FCSTD DOCUMENT  (FreeCAD 0.20R29177 +426 (Git))
Label: X2SON-5_0.8x0.8mm_P0.48mm
License: All rights reserved
LicenseURL: http://en.wikipedia.org/wiki/All_rights_reserved
objects: Sketcher::SketchObject×14, App::Annotation×2, Part::Offset2D×2, App::DocumentObjectGroup×1
note: 16 computed .brp shape members not serialized (recipe doc carries the construction recipe); baked Part::Feature solids carry a one-line shape summary decoded from their .brp

FEATURE [Sketcher::SketchObject] Sketch  label="Pads_Poly_Mask1"
  FullyConstrained = true
  sketch-geometry (12):
    g0: LineSegment StartX=-0.55 StartY=0.13 StartZ=0 EndX=-0.34 EndY=0.13 EndZ=0
    g1: LineSegment StartX=-0.34 StartY=0.13 StartZ=0 EndX=-0.18 EndY=0.29 EndZ=0
    g2: LineSegment StartX=-0.18 StartY=0.29 StartZ=0 EndX=-0.18 EndY=0.35 EndZ=0
    g3: LineSegment StartX=-0.18 StartY=0.35 StartZ=0 EndX=-0.55 EndY=0.35 EndZ=0
    g4: LineSegment StartX=-0.6 StartY=0.3 StartZ=0 EndX=-0.6 EndY=0.18 EndZ=0
    g5: LineSegment StartX=-0.39 StartY=0.35 StartZ=0 EndX=-0.39 EndY=0.13 EndZ=0
    g6: LineSegment StartX=-0.6 StartY=0.24 StartZ=0 EndX=-0.23 EndY=0.24 EndZ=0
    g7: Circle CenterX=-0.39 CenterY=0.24 CenterZ=0 NormalX=0 NormalY=0 NormalZ=1 AngleXU=0 Radius=0.025
    g8: ArcOfCircle CenterX=-0.55 CenterY=0.3 CenterZ=0 NormalX=0 NormalY=0 NormalZ=1 AngleXU=0 Radius=0.05 StartAngle=1.5708 EndAngle=3.14159
    g9: GeomPoint X=-0.6 Y=0.35 Z=0
    g10: ArcOfCircle CenterX=-0.55 CenterY=0.18 CenterZ=0 NormalX=0 NormalY=0 NormalZ=1 AngleXU=0 Radius=0.05 StartAngle=3.14159 EndAngle=4.71239
    g11: GeomPoint X=-0.6 Y=0.13 Z=0
  constraints (32):
    c: Horizontal(g0)
    c: Coincident(g0,g1)
    c: Coincident(g1,g2)
    c: Vertical(g2)
    c: Coincident(g2,g3)
    c: Horizontal(g3)
    c: Vertical(g4)
    c: Distance(g3,g9) = 0.42
    c: Distance(g0,g11) = 0.26
    c: Distance(g11,g9) = 0.22
    c: Distance(g2) = 0.06
    c: PointOnObject(g5,g0)
    c: Vertical(g5)
    c: Symmetric(g3,g9,g5)
    c: PointOnObject(g6,g1)
    c: Horizontal(g6)
    c: Symmetric(g9,g11,g6)
    c: Distance(g6,g-1) = 0.24
    c: PointOnObject(g7,g6)
    c: PointOnObject(g7,g5)
    c: Diameter(g7) = 0.05
    c: PointOnObject(g9,g3)
    c: PointOnObject(g9,g4)
    c: Tangent(g3,g8) = -1.5708
    c: Tangent(g4,g8) = -1.5708
    c: PointOnObject(g11,g4)
    c: PointOnObject(g11,g0)
    c: Tangent(g4,g10) = -1.5708
    c: Tangent(g0,g10) = -1.5708
    c: Radius(g10) = 0.05
    c: Radius(g8) = 0.05
    c: Distance(g5,g-2) = 0.39
FEATURE [App::Annotation] Text  label="Ref#_1.0mm"
  LabelText = REF**
  Position = (0,1.5,0)
FEATURE [App::Annotation] Text001  label="Value#_0.6mm"
  LabelText = X2SON-4_0.8x0.8mm_P0.48mm
  Position = (0,-1.5,0)
FEATURE [Sketcher::SketchObject] Sketch001  label="Pads_Poly_Mask3"
  FullyConstrained = true
  sketch-geometry (13):
    g0: LineSegment StartX=-0.141421 StartY=0.0353553 StartZ=0 EndX=-0.0353553 EndY=0.141421 EndZ=0
    g1: LineSegment StartX=0.0353553 StartY=0.141421 StartZ=0 EndX=0.141421 EndY=0.0353553 EndZ=0
    g2: LineSegment StartX=0.141421 StartY=-0.0353553 StartZ=0 EndX=0.0353553 EndY=-0.141421 EndZ=0
    g3: LineSegment StartX=-0.0353553 StartY=-0.141421 StartZ=0 EndX=-0.141421 EndY=-0.0353553 EndZ=0
    g4: ArcOfCircle CenterX=0 CenterY=0.106066 CenterZ=0 NormalX=0 NormalY=0 NormalZ=1 AngleXU=0 Radius=0.05 StartAngle=0.785398 EndAngle=2.35619
    g5: GeomPoint X=0 Y=0.176777 Z=0
    g6: ArcOfCircle CenterX=-0.106066 CenterY=-1e-16 CenterZ=0 NormalX=0 NormalY=0 NormalZ=1 AngleXU=0 Radius=0.05 StartAngle=2.35619 EndAngle=3.92699
    g7: GeomPoint X=-0.176777 Y=0 Z=0
    g8: ArcOfCircle CenterX=0 CenterY=-0.106066 CenterZ=0 NormalX=0 NormalY=0 NormalZ=1 AngleXU=0 Radius=0.05 StartAngle=3.92699 EndAngle=5.49779
    g9: GeomPoint X=0 Y=-0.176777 Z=0
    g10: ArcOfCircle CenterX=0.106066 CenterY=0 CenterZ=0 NormalX=0 NormalY=0 NormalZ=1 AngleXU=0 Radius=0.05 StartAngle=5.49779 EndAngle=7.06858
    g11: GeomPoint X=0.176777 Y=0 Z=0
    g12: Circle CenterX=0 CenterY=0 CenterZ=0 NormalX=0 NormalY=0 NormalZ=1 AngleXU=0 Radius=0.025
  constraints (31):
    c: PointOnObject(g7,g-1)
    c: PointOnObject(g5,g-2)
    c: PointOnObject(g11,g-1)
    c: PointOnObject(g9,g-2)
    c: Perpendicular(g1,g0)
    c: Perpendicular(g2,g1)
    c: Perpendicular(g3,g2)
    c: Distance(g11,g5) = 0.25
    c: PointOnObject(g5,g0)
    c: PointOnObject(g5,g1)
    c: Tangent(g0,g4) = 1.5708
    c: Tangent(g1,g4) = 1.5708
    c: Radius(g4) = 0.05
    c: PointOnObject(g7,g0)
    c: PointOnObject(g7,g3)
    c: Tangent(g0,g6) = 1.5708
    c: Tangent(g3,g6) = 1.5708
    c: PointOnObject(g9,g3)
    c: PointOnObject(g9,g2)
    c: Tangent(g3,g8) = 1.5708
    c: Tangent(g2,g8) = 1.5708
    c: PointOnObject(g11,g2)
    c: PointOnObject(g11,g1)
    c: Tangent(g2,g10) = 1.5708
    c: Tangent(g1,g10) = 1.5708
    c: Equal(g4,g10)
    c: Equal(g4,g8)
    c: Equal(g4,g6)
    c: Coincident(g12,g-1)
    c: Diameter(g12) = 0.05
    c: Distance(g1,g3) = 0.25
FEATURE [Sketcher::SketchObject] MirroredSketch001  label="Pads_Poly_Mask5"
  FullyConstrained = true
  sketch-geometry (12):
    g0: LineSegment StartX=0.55 StartY=0.13 StartZ=0 EndX=0.34 EndY=0.13 EndZ=0
    g1: LineSegment StartX=0.34 StartY=0.13 StartZ=0 EndX=0.18 EndY=0.29 EndZ=0
    g2: LineSegment StartX=0.18 StartY=0.29 StartZ=0 EndX=0.18 EndY=0.35 EndZ=0
    g3: LineSegment StartX=0.18 StartY=0.35 StartZ=0 EndX=0.55 EndY=0.35 EndZ=0
    g4: LineSegment StartX=0.6 StartY=0.3 StartZ=0 EndX=0.6 EndY=0.18 EndZ=0
    g5: LineSegment StartX=0.39 StartY=0.35 StartZ=0 EndX=0.39 EndY=0.13 EndZ=0
    g6: LineSegment StartX=0.6 StartY=0.24 StartZ=0 EndX=0.23 EndY=0.24 EndZ=0
    g7: Circle CenterX=0.39 CenterY=0.24 CenterZ=0 NormalX=0 NormalY=0 NormalZ=1 AngleXU=0 Radius=0.025
    g8: ArcOfCircle CenterX=0.55 CenterY=0.3 CenterZ=0 NormalX=0 NormalY=0 NormalZ=1 AngleXU=0 Radius=0.05 StartAngle=0 EndAngle=1.5708
    g9: GeomPoint X=0.6 Y=0.35 Z=0
    g10: ArcOfCircle CenterX=0.55 CenterY=0.18 CenterZ=0 NormalX=0 NormalY=0 NormalZ=1 AngleXU=0 Radius=0.05 StartAngle=4.71239 EndAngle=6.28319
    g11: GeomPoint X=0.6 Y=0.13 Z=0
  constraints (32):
    c: Horizontal(g0)
    c: Coincident(g0,g1)
    c: Coincident(g1,g2)
    c: Vertical(g2)
    c: Coincident(g2,g3)
    c: Horizontal(g3)
    c: Vertical(g4)
    c: Distance(g3,g9) = 0.42
    c: Distance(g0,g11) = 0.26
    c: Distance(g11,g9) = 0.22
    c: Distance(g2) = 0.06
    c: PointOnObject(g5,g0)
    c: Vertical(g5)
    c: Symmetric(g3,g9,g5)
    c: PointOnObject(g6,g1)
    c: Horizontal(g6)
    c: Symmetric(g9,g11,g6)
    c: PointOnObject(g7,g6)
    c: PointOnObject(g7,g5)
    c: Diameter(g7) = 0.05
    c: PointOnObject(g9,g3)
    c: PointOnObject(g9,g4)
    c: Tangent(g3,g8) = 1.5708
    c: Tangent(g4,g8) = 1.5708
    c: PointOnObject(g11,g4)
    c: PointOnObject(g11,g0)
    c: Tangent(g4,g10) = 1.5708
    c: Tangent(g0,g10) = 1.5708
    c: Radius(g10) = 0.05
    c: Radius(g8) = 0.05
    c: Distance(g5,g-2) = 0.39
    c: Distance(g6,g-1) = 0.24
FEATURE [Sketcher::SketchObject] Sketch003  label="Pads_TH_SMD_padNum=3"
  FullyConstrained = true
  sketch-geometry (2):
    g0: Circle CenterX=0 CenterY=0 CenterZ=0 NormalX=0 NormalY=0 NormalZ=1 AngleXU=0 Radius=0.051
    g1: Circle CenterX=0 CenterY=0 CenterZ=0 NormalX=0 NormalY=0 NormalZ=1 AngleXU=0 Radius=0.1525
  constraints (4):
    c: Coincident(g0,g-1)
    c: Coincident(g1,g0)
    c: Diameter(g0) = 0.102
    c: Diameter(g1) = 0.305
FEATURE [Part::Offset2D] Offset2D001  label="Offset2D"
  Fill = false
  Intersection = false
  Join = 1
  Mode = 1
  SelfIntersection = false
  Source = -> Sketch
  Value = 0.05
FEATURE [Sketcher::SketchObject] Sketch007  label="Pads_Poly_padNum=1"
  ExternalGeometry = -> [Sketch]
  FullyConstrained = true
  sketch-geometry (9):
    g0: LineSegment StartX=-0.55 StartY=0.08 StartZ=0 EndX=-0.319289 EndY=0.08 EndZ=0
    g1: LineSegment StartX=-0.319289 StartY=0.08 StartZ=0 EndX=-0.13 EndY=0.269289 EndZ=0
    g2: LineSegment StartX=-0.13 StartY=0.269289 StartZ=0 EndX=-0.13 EndY=0.4 EndZ=0
    g3: LineSegment StartX=-0.13 StartY=0.4 StartZ=0 EndX=-0.55 EndY=0.4 EndZ=0
    g4: ArcOfCircle CenterX=-0.55 CenterY=0.3 CenterZ=0 NormalX=0 NormalY=0 NormalZ=1 AngleXU=0 Radius=0.1 StartAngle=1.5708 EndAngle=3.14159
    g5: LineSegment StartX=-0.65 StartY=0.3 StartZ=0 EndX=-0.65 EndY=0.18 EndZ=0
    g6: ArcOfCircle CenterX=-0.55 CenterY=0.18 CenterZ=0 NormalX=0 NormalY=0 NormalZ=1 AngleXU=0 Radius=0.1 StartAngle=3.14159 EndAngle=4.71239
    g7: Circle CenterX=-0.39 CenterY=0.24 CenterZ=0 NormalX=0 NormalY=0 NormalZ=1 AngleXU=0 Radius=0.075
    g8: LineSegment StartX=-0.34 StartY=0.13 StartZ=0 EndX=-0.304645 EndY=0.0946447 EndZ=0
  constraints (26):
    c: Horizontal(g0)
    c: Coincident(g0,g1)
    c: Coincident(g1,g2)
    c: Vertical(g2)
    c: Coincident(g2,g3)
    c: Horizontal(g3)
    c: Coincident(g3,g4)
    c: Coincident(g4,g5)
    c: Vertical(g5)
    c: Coincident(g5,g6)
    c: Coincident(g6,g0)
    c: DistanceY(g-7,g2) = 0.05
    c: DistanceX(g5,g-9) = 0.05
    c: Radius(g6) = 0.1
    c: Radius(g4) = 0.1
    c: Distance(g-7,g2) = 0.05
    c: Distance(g-6,g0) = 0.05
    c: Coincident(g4,g-8)
    c: Coincident(g6,g-9)
    c: Parallel(g1,g-6)
    c: Perpendicular(g8,g1)
    c: Coincident(g8,g-6)
    c: PointOnObject(g8,g1)
    c: Distance(g8) = 0.05
    c: Diameter(g7) = 0.15
    c: Coincident(g7,g-10)
FEATURE [Sketcher::SketchObject] MirroredSketch  label="Pads_Poly_padNum=5"
  ExternalGeometry = -> [Sketch007,MirroredSketch001]
  FullyConstrained = true
  sketch-geometry (9):
    g0: LineSegment StartX=0.55 StartY=0.08 StartZ=0 EndX=0.319289 EndY=0.08 EndZ=0
    g1: LineSegment StartX=0.319289 StartY=0.08 StartZ=0 EndX=0.13 EndY=0.269289 EndZ=0
    g2: LineSegment StartX=0.13 StartY=0.269289 StartZ=0 EndX=0.13 EndY=0.4 EndZ=0
    g3: LineSegment StartX=0.13 StartY=0.4 StartZ=0 EndX=0.55 EndY=0.4 EndZ=0
    g4: ArcOfCircle CenterX=0.55 CenterY=0.3 CenterZ=0 NormalX=0 NormalY=0 NormalZ=1 AngleXU=0 Radius=0.1 StartAngle=2.77023e-08 EndAngle=1.5708
    g5: LineSegment StartX=0.65 StartY=0.3 StartZ=0 EndX=0.65 EndY=0.18 EndZ=0
    g6: ArcOfCircle CenterX=0.55 CenterY=0.18 CenterZ=0 NormalX=0 NormalY=0 NormalZ=1 AngleXU=0 Radius=0.1 StartAngle=4.71239 EndAngle=6.28319
    g7: Circle CenterX=0.39 CenterY=0.24 CenterZ=0 NormalX=0 NormalY=0 NormalZ=1 AngleXU=0 Radius=0.075
    g8: LineSegment StartX=0.34 StartY=0.13 StartZ=0 EndX=0.304645 EndY=0.0946447 EndZ=0
  constraints (22):
    c: Horizontal(g0)
    c: Coincident(g0,g1)
    c: Coincident(g1,g2)
    c: Coincident(g2,g3)
    c: Horizontal(g3)
    c: Coincident(g3,g4)
    c: Coincident(g4,g5)
    c: Vertical(g5)
    c: Coincident(g5,g6)
    c: Coincident(g6,g0)
    c: Perpendicular(g8,g1)
    c: PointOnObject(g8,g1)
    c: Diameter(g7) = 0.15
    c: Symmetric(g-4,g2,g-2)
    c: Symmetric(g4,g-6,g-2)
    c: Symmetric(g0,g-9,g-2)
    c: Symmetric(g1,g-9,g-2)
    c: Equal(g6,g-7)
    c: Symmetric(g7,g-10,g-2)
    c: Symmetric(g6,g-7,g-2)
    c: Symmetric(g4,g-5,g-2)
    c: Coincident(g8,g-11)
FEATURE [Sketcher::SketchObject] MirroredSketch002  label="Pads_Poly_Mask4"
  FullyConstrained = true
  sketch-geometry (12):
    g0: LineSegment StartX=0.55 StartY=-0.13 StartZ=0 EndX=0.34 EndY=-0.13 EndZ=0
    g1: LineSegment StartX=0.34 StartY=-0.13 StartZ=0 EndX=0.18 EndY=-0.29 EndZ=0
    g2: LineSegment StartX=0.18 StartY=-0.29 StartZ=0 EndX=0.18 EndY=-0.35 EndZ=0
    g3: LineSegment StartX=0.18 StartY=-0.35 StartZ=0 EndX=0.55 EndY=-0.35 EndZ=0
    g4: LineSegment StartX=0.6 StartY=-0.3 StartZ=0 EndX=0.6 EndY=-0.18 EndZ=0
    g5: LineSegment StartX=0.39 StartY=-0.35 StartZ=0 EndX=0.39 EndY=-0.13 EndZ=0
    g6: LineSegment StartX=0.6 StartY=-0.24 StartZ=0 EndX=0.23 EndY=-0.24 EndZ=0
    g7: Circle CenterX=0.39 CenterY=-0.24 CenterZ=0 NormalX=0 NormalY=0 NormalZ=1 AngleXU=0 Radius=0.025
    g8: ArcOfCircle CenterX=0.55 CenterY=-0.3 CenterZ=0 NormalX=0 NormalY=0 NormalZ=1 AngleXU=0 Radius=0.05 StartAngle=4.71239 EndAngle=6.28319
    g9: GeomPoint X=0.6 Y=-0.35 Z=0
    g10: ArcOfCircle CenterX=0.55 CenterY=-0.18 CenterZ=0 NormalX=0 NormalY=0 NormalZ=1 AngleXU=0 Radius=0.05 StartAngle=0 EndAngle=1.5708
    g11: GeomPoint X=0.6 Y=-0.13 Z=0
  constraints (32):
    c: Horizontal(g0)
    c: Coincident(g0,g1)
    c: Coincident(g1,g2)
    c: Vertical(g2)
    c: Coincident(g2,g3)
    c: Horizontal(g3)
    c: Vertical(g4)
    c: Distance(g3,g9) = 0.42
    c: Distance(g0,g11) = 0.26
    c: Distance(g11,g9) = 0.22
    c: Distance(g2) = 0.06
    c: PointOnObject(g5,g0)
    c: Vertical(g5)
    c: Symmetric(g3,g9,g5)
    c: PointOnObject(g6,g1)
    c: Horizontal(g6)
    c: Symmetric(g9,g11,g6)
    c: PointOnObject(g7,g6)
    c: PointOnObject(g7,g5)
    c: Diameter(g7) = 0.05
    c: PointOnObject(g9,g3)
    c: PointOnObject(g9,g4)
    c: Tangent(g3,g8) = -1.5708
    c: Tangent(g4,g8) = -1.5708
    c: PointOnObject(g11,g4)
    c: PointOnObject(g11,g0)
    c: Tangent(g4,g10) = -1.5708
    c: Tangent(g0,g10) = -1.5708
    c: Radius(g10) = 0.05
    c: Radius(g8) = 0.05
    c: Distance(g6,g-1) = 0.24
    c: Distance(g5,g-2) = 0.39
FEATURE [Sketcher::SketchObject] MirroredSketch004  label="Pads_Poly_padNum=4"
  ExternalGeometry = -> [MirroredSketch,MirroredSketch002]
  FullyConstrained = true
  sketch-geometry (9):
    g0: LineSegment StartX=0.55 StartY=-0.08 StartZ=0 EndX=0.319289 EndY=-0.08 EndZ=0
    g1: LineSegment StartX=0.319289 StartY=-0.08 StartZ=0 EndX=0.13 EndY=-0.269289 EndZ=0
    g2: LineSegment StartX=0.13 StartY=-0.269289 StartZ=0 EndX=0.13 EndY=-0.4 EndZ=0
    g3: LineSegment StartX=0.13 StartY=-0.4 StartZ=0 EndX=0.55 EndY=-0.4 EndZ=0
    g4: ArcOfCircle CenterX=0.55 CenterY=-0.3 CenterZ=0 NormalX=0 NormalY=0 NormalZ=1 AngleXU=0 Radius=0.1 StartAngle=4.71239 EndAngle=6.28319
    g5: LineSegment StartX=0.65 StartY=-0.3 StartZ=0 EndX=0.65 EndY=-0.18 EndZ=0
    g6: ArcOfCircle CenterX=0.55 CenterY=-0.18 CenterZ=0 NormalX=0 NormalY=0 NormalZ=1 AngleXU=0 Radius=0.1 StartAngle=3.56978e-08 EndAngle=1.5708
    g7: Circle CenterX=0.39 CenterY=-0.24 CenterZ=0 NormalX=0 NormalY=0 NormalZ=1 AngleXU=0 Radius=0.075
    g8: LineSegment StartX=0.34 StartY=-0.13 StartZ=0 EndX=0.304645 EndY=-0.0946447 EndZ=0
  constraints (23):
    c: Horizontal(g0)
    c: Coincident(g0,g1)
    c: Coincident(g1,g2)
    c: Coincident(g2,g3)
    c: Horizontal(g3)
    c: Coincident(g3,g4)
    c: Coincident(g4,g5)
    c: Coincident(g5,g6)
    c: Coincident(g6,g0)
    c: Perpendicular(g8,g1)
    c: PointOnObject(g8,g1)
    c: Distance(g8) = 0.05
    c: Diameter(g7) = 0.15
    c: Symmetric(g4,g-4,g-1)
    c: Equal(g4,g-4)
    c: Symmetric(g2,g-6,g-1)
    c: Equal(g0,g-8)
    c: Symmetric(g5,g-3,g-1)
    c: Symmetric(g6,g-3,g-1)
    c: Symmetric(g-4,g4,g-1)
    c: Symmetric(g-9,g7,g-1)
    c: Symmetric(g1,g-7,g-1)
    c: Equal(g-8,g0)
FEATURE [Sketcher::SketchObject] MirroredSketch005  label="Pads_Poly_Mask2"
  FullyConstrained = true
  sketch-geometry (12):
    g0: LineSegment StartX=-0.55 StartY=-0.13 StartZ=0 EndX=-0.34 EndY=-0.13 EndZ=0
    g1: LineSegment StartX=-0.34 StartY=-0.13 StartZ=0 EndX=-0.18 EndY=-0.29 EndZ=0
    g2: LineSegment StartX=-0.18 StartY=-0.29 StartZ=0 EndX=-0.18 EndY=-0.35 EndZ=0
    g3: LineSegment StartX=-0.18 StartY=-0.35 StartZ=0 EndX=-0.55 EndY=-0.35 EndZ=0
    g4: LineSegment StartX=-0.6 StartY=-0.3 StartZ=0 EndX=-0.6 EndY=-0.18 EndZ=0
    g5: LineSegment StartX=-0.39 StartY=-0.35 StartZ=0 EndX=-0.39 EndY=-0.13 EndZ=0
    g6: LineSegment StartX=-0.6 StartY=-0.24 StartZ=0 EndX=-0.23 EndY=-0.24 EndZ=0
    g7: Circle CenterX=-0.39 CenterY=-0.24 CenterZ=0 NormalX=0 NormalY=0 NormalZ=1 AngleXU=0 Radius=0.025
    g8: ArcOfCircle CenterX=-0.55 CenterY=-0.3 CenterZ=0 NormalX=0 NormalY=0 NormalZ=1 AngleXU=0 Radius=0.05 StartAngle=3.14159 EndAngle=4.71239
    g9: GeomPoint X=-0.6 Y=-0.35 Z=0
    g10: ArcOfCircle CenterX=-0.55 CenterY=-0.18 CenterZ=0 NormalX=0 NormalY=0 NormalZ=1 AngleXU=0 Radius=0.05 StartAngle=1.5708 EndAngle=3.14159
    g11: GeomPoint X=-0.6 Y=-0.13 Z=0
  constraints (32):
    c: Horizontal(g0)
    c: Coincident(g0,g1)
    c: Coincident(g1,g2)
    c: Vertical(g2)
    c: Coincident(g2,g3)
    c: Horizontal(g3)
    c: Vertical(g4)
    c: Distance(g3,g9) = 0.42
    c: Distance(g0,g11) = 0.26
    c: Distance(g11,g9) = 0.22
    c: Distance(g2) = 0.06
    c: PointOnObject(g5,g0)
    c: Vertical(g5)
    c: Symmetric(g3,g9,g5)
    c: PointOnObject(g6,g1)
    c: Horizontal(g6)
    c: Symmetric(g9,g11,g6)
    c: PointOnObject(g7,g6)
    c: PointOnObject(g7,g5)
    c: Diameter(g7) = 0.05
    c: PointOnObject(g9,g3)
    c: PointOnObject(g9,g4)
    c: Tangent(g3,g8) = 1.5708
    c: Tangent(g4,g8) = 1.5708
    c: PointOnObject(g11,g4)
    c: PointOnObject(g11,g0)
    c: Tangent(g4,g10) = 1.5708
    c: Tangent(g0,g10) = 1.5708
    c: Radius(g10) = 0.05
    c: Radius(g8) = 0.05
    c: Distance(g6,g-1) = 0.24
    c: Distance(g5,g-2) = 0.39
FEATURE [Sketcher::SketchObject] MirroredSketch003  label="Pads_Poly_padNum=2"
  ExternalGeometry = -> [Sketch007,Sketch,MirroredSketch005]
  FullyConstrained = true
  sketch-geometry (9):
    g0: LineSegment StartX=-0.55 StartY=-0.08 StartZ=0 EndX=-0.319289 EndY=-0.08 EndZ=0
    g1: LineSegment StartX=-0.319289 StartY=-0.08 StartZ=0 EndX=-0.13 EndY=-0.269289 EndZ=0
    g2: LineSegment StartX=-0.13 StartY=-0.269289 StartZ=0 EndX=-0.13 EndY=-0.4 EndZ=0
    g3: LineSegment StartX=-0.13 StartY=-0.4 StartZ=0 EndX=-0.55 EndY=-0.4 EndZ=0
    g4: ArcOfCircle CenterX=-0.55 CenterY=-0.3 CenterZ=0 NormalX=0 NormalY=0 NormalZ=1 AngleXU=0 Radius=0.1 StartAngle=3.14159 EndAngle=4.71239
    g5: LineSegment StartX=-0.65 StartY=-0.3 StartZ=0 EndX=-0.65 EndY=-0.18 EndZ=0
    g6: ArcOfCircle CenterX=-0.55 CenterY=-0.18 CenterZ=0 NormalX=0 NormalY=0 NormalZ=1 AngleXU=0 Radius=0.1 StartAngle=1.5708 EndAngle=3.14159
    g7: Circle CenterX=-0.39 CenterY=-0.24 CenterZ=0 NormalX=0 NormalY=0 NormalZ=1 AngleXU=0 Radius=0.075
    g8: LineSegment StartX=-0.34 StartY=-0.13 StartZ=0 EndX=-0.304645 EndY=-0.0946447 EndZ=0
  constraints (22):
    c: Coincident(g0,g1)
    c: Coincident(g1,g2)
    c: Vertical(g2)
    c: Coincident(g2,g3)
    c: Horizontal(g3)
    c: Coincident(g3,g4)
    c: Coincident(g4,g5)
    c: Vertical(g5)
    c: Coincident(g5,g6)
    c: Coincident(g6,g0)
    c: Perpendicular(g8,g1)
    c: PointOnObject(g8,g1)
    c: Diameter(g7) = 0.15
    c: Symmetric(g-3,g6,g-1)
    c: Symmetric(g-4,g4,g-1)
    c: Symmetric(g-7,g0,g-1)
    c: Symmetric(g7,g-11,g-1)
    c: Equal(g5,g-6)
    c: Symmetric(g3,g-5,g-1)
    c: Symmetric(g0,g-8,g-1)
    c: Symmetric(g1,g-9,g-1)
    c: Coincident(g8,g-13)
FEATURE [Sketcher::SketchObject] Sketch008  label="F_Fab_0.1"
  FullyConstrained = true
  sketch-geometry (8):
    g0: LineSegment StartX=0.4 StartY=0.4 StartZ=0 EndX=0.4 EndY=-0.4 EndZ=0
    g1: LineSegment StartX=0.4 StartY=-0.4 StartZ=0 EndX=-0.4 EndY=-0.4 EndZ=0
    g2: GeomPoint X=0 Y=0 Z=0
    g3: LineSegment StartX=-0.4 StartY=0.2 StartZ=0 EndX=-0.2 EndY=0.4 EndZ=0
    g4: LineSegment StartX=-0.4 StartY=0.4 StartZ=0 EndX=-0.2 EndY=0.4 EndZ=0
    g5: LineSegment StartX=-0.2 StartY=0.4 StartZ=0 EndX=0.4 EndY=0.4 EndZ=0
    g6: LineSegment StartX=-0.4 StartY=-0.4 StartZ=0 EndX=-0.4 EndY=0.2 EndZ=0
    g7: LineSegment StartX=-0.4 StartY=0.2 StartZ=0 EndX=-0.4 EndY=0.4 EndZ=0
  constraints (20):
    c: Coincident(g7,g4)
    c: Coincident(g5,g0)
    c: Coincident(g0,g1)
    c: Coincident(g1,g6)
    c: Horizontal(g1)
    c: Vertical(g0)
    c: Symmetric(g5,g6,g2)
    c: Coincident(g2,g-1)
    c: Distance(g0) = 0.8
    c: Distance(g3,g7) = 0.2
    c: Distance(g3,g7) = 0.2
    c: Coincident(g4,g5)
    c: Horizontal(g4)
    c: Horizontal(g5)
    c: Distance(g4,g5) = 0.8
    c: Coincident(g3,g4)
    c: Coincident(g6,g7)
    c: Vertical(g6)
    c: Vertical(g7)
    c: Coincident(g3,g6)
FEATURE [Sketcher::SketchObject] Sketch009  label="F_CrtYd_0.05"
  ExternalGeometry = -> [MirroredSketch]
  FullyConstrained = true
  sketch-geometry (5):
    g0: LineSegment StartX=-0.9 StartY=-0.65 StartZ=0 EndX=-0.9 EndY=0.65 EndZ=0
    g1: LineSegment StartX=-0.9 StartY=0.65 StartZ=0 EndX=0.9 EndY=0.65 EndZ=0
    g2: LineSegment StartX=0.9 StartY=0.65 StartZ=0 EndX=0.9 EndY=-0.65 EndZ=0
    g3: LineSegment StartX=0.9 StartY=-0.65 StartZ=0 EndX=-0.9 EndY=-0.65 EndZ=0
    g4: GeomPoint X=0 Y=0 Z=0
  constraints (12):
    c: Coincident(g0,g1)
    c: Coincident(g1,g2)
    c: Coincident(g2,g3)
    c: Coincident(g3,g0)
    c: Horizontal(g1)
    c: Horizontal(g3)
    c: Vertical(g0)
    c: Vertical(g2)
    c: Symmetric(g1,g0,g4)
    c: Coincident(g4,g-1)
    c: Distance(g-3,g1) = 0.25
    c: Distance(g-4,g2) = 0.25
FEATURE [Sketcher::SketchObject] Sketch010  label="F_Silks_0.12"
  ExternalGeometry = -> [Sketch007,Sketch008]
  FullyConstrained = true
  sketch-geometry (2):
    g0: LineSegment StartX=-0.65 StartY=0.55 StartZ=0 EndX=0.4 EndY=0.55 EndZ=0
    g1: LineSegment StartX=-0.4 StartY=-0.55 StartZ=0 EndX=0.4 EndY=-0.55 EndZ=0
  constraints (8):
    c: Horizontal(g0)
    c: Distance(g-3,g0) = 0.15
    c: Vertical(g0,g-5)
    c: Vertical(g-4,g0)
    c: Horizontal(g1)
    c: Distance(g-6,g1) = 0.15
    c: Vertical(g-6,g1)
    c: Vertical(g1,g-6)
FEATURE [Part::Offset2D] Offset2D  label="Offset2D001"
  Fill = false
  Intersection = false
  Join = 1
  Mode = 1
  SelfIntersection = false
  Source = -> Sketch001
  Value = 0.05
FEATURE [Sketcher::SketchObject] Sketch011  label="Pads_Poly_padNum=3"
  ExternalGeometry = -> [Sketch001]
  FullyConstrained = true
  sketch-geometry (9):
    g0: LineSegment StartX=-0.176777 StartY=0.0707107 StartZ=0 EndX=-0.0707107 EndY=0.176777 EndZ=0
    g1: ArcOfCircle CenterX=0 CenterY=0.106066 CenterZ=0 NormalX=0 NormalY=0 NormalZ=1 AngleXU=0 Radius=0.1 StartAngle=0.785398 EndAngle=2.35619
    g2: LineSegment StartX=0.0707107 StartY=0.176777 StartZ=0 EndX=0.176777 EndY=0.0707107 EndZ=0
    g3: ArcOfCircle CenterX=0.106066 CenterY=0 CenterZ=0 NormalX=0 NormalY=0 NormalZ=1 AngleXU=0 Radius=0.1 StartAngle=5.49778 EndAngle=7.06858
    g4: LineSegment StartX=0.176776 StartY=-0.0707109 StartZ=0 EndX=0.0707104 EndY=-0.176777 EndZ=0
    g5: ArcOfCircle CenterX=0 CenterY=-0.106066 CenterZ=0 NormalX=0 NormalY=0 NormalZ=1 AngleXU=0 Radius=0.1 StartAngle=3.92697 EndAngle=5.49778
    g6: LineSegment StartX=-0.0707121 StartY=-0.176775 StartZ=0 EndX=-0.176778 EndY=-0.0707092 EndZ=0
    g7: ArcOfCircle CenterX=-0.106066 CenterY=-1e-16 CenterZ=0 NormalX=0 NormalY=0 NormalZ=1 AngleXU=0 Radius=0.1 StartAngle=2.35619 EndAngle=3.92697
    g8: Circle CenterX=0 CenterY=0 CenterZ=0 NormalX=0 NormalY=0 NormalZ=1 AngleXU=0 Radius=0.075
  constraints (26):
    c: Coincident(g0,g1)
    c: Coincident(g1,g2)
    c: Coincident(g2,g3)
    c: Coincident(g3,g4)
    c: Coincident(g4,g5)
    c: Coincident(g5,g6)
    c: Coincident(g6,g7)
    c: Coincident(g7,g0)
    c: Diameter(g8) = 0.15
    c: Equal(g1,g3)
    c: Equal(g3,g5)
    c: Equal(g5,g7)
    c: Radius(g1) = 0.1
    c: Parallel(g0,g-4)
    c: Parallel(g-5,g6)
    c: Parallel(g-6,g4)
    c: Parallel(g2,g-3)
    c: Coincident(g5,g-10)
    c: Coincident(g3,g-7)
    c: Coincident(g-8,g1)
    c: Coincident(g7,g-9)
    c: Distance(g-8,g2) = 0.05
    c: Distance(g-8,g0) = 0.05
    c: Distance(g-9,g6) = 0.05
    c: Distance(g-10,g4) = 0.05
    c: Coincident(g8,g-1)
FEATURE [App::DocumentObjectGroup] Group  label="X2SON-5_0.8x0.8mm_P0.48mm"
  Group = -> [Sketch007,Text001,Sketch,MirroredSketch001,Sketch001,Sketch003,MirroredSketch002,Text,MirroredSketch,MirroredSketch005,MirroredSketch003,MirroredSketch004,Sketch008,Sketch009,Sketch010,Sketch011]
